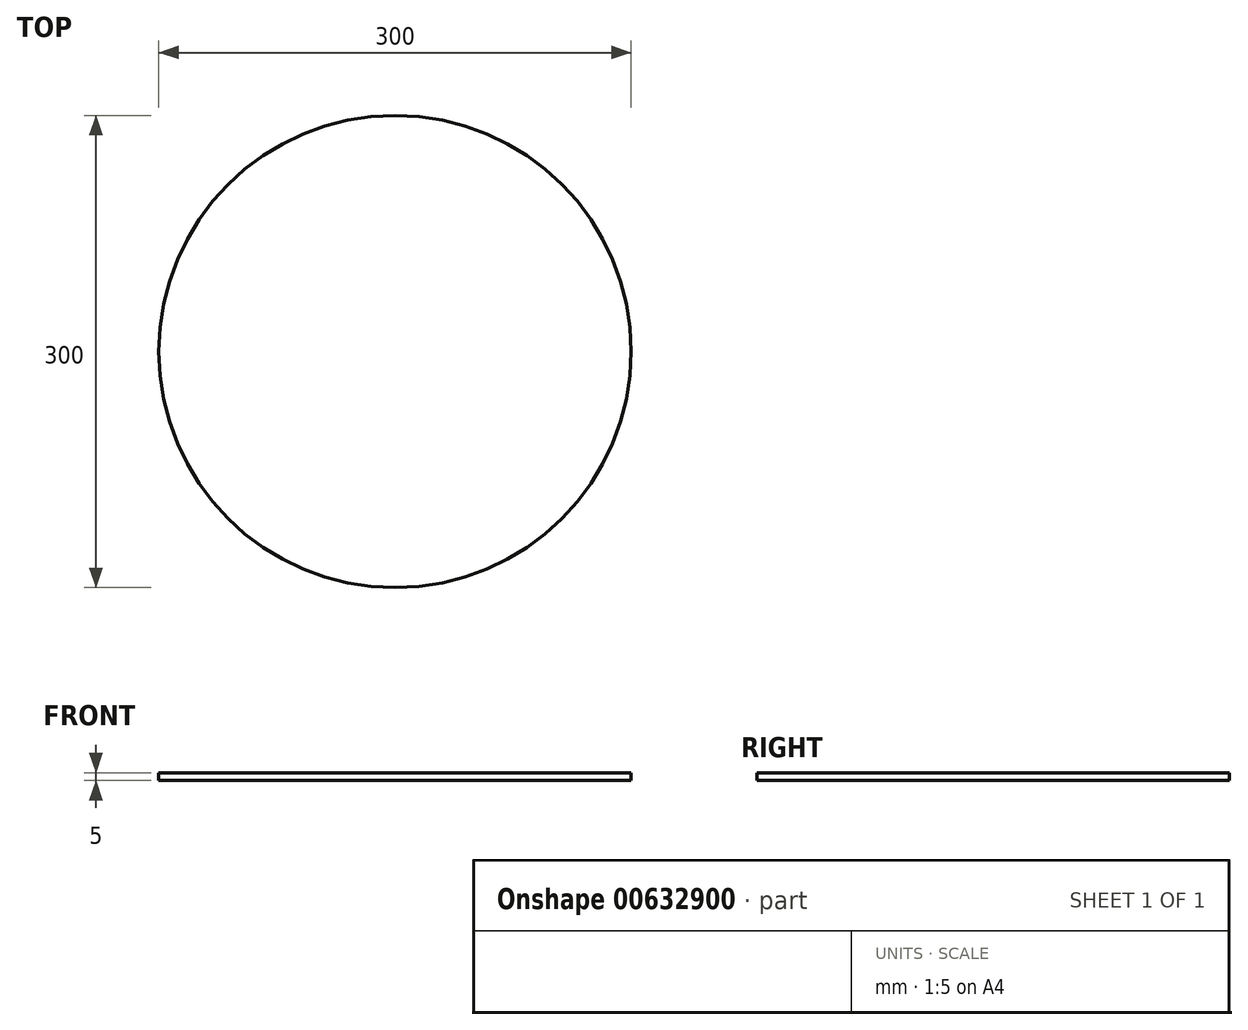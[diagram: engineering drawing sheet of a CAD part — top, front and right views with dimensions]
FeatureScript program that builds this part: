
annotation { "Feature Type Name" : "Feature", "Feature Type Description" : "" }
export const myFeature = defineFeature(function(context is Context, id is Id, definition is map)
    precondition{}
    {
        {
            var Q0;
            Q0=qCreatedBy(makeId("Top.planeOp"),FACE);
            var sketch = newSketch(context, id + "F0", { "sketchPlane" : qUnion([Q0])});
            skCircle(sketch, "E0", {"center": v(0, 0) * mm, "radius": 150 * mm});
            skSolve(sketch);
        }
        {
            var Q0;
            Q0=makeQuery(id+"F0.imprint","IMPRINT",FACE,{"disambiguationData":[TD([[makeQuery(id+"F0.imprint","IMPRINT",EDGE,{"derivedFrom":sQuery(id+"F0.wireOp",EDGE,"E0")}),1.0]])]});
            extrude(context, id + "F1", {"entities" : qUnion([Q0]), "depth" : 5 * mm});
        }
    });
